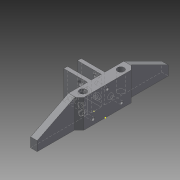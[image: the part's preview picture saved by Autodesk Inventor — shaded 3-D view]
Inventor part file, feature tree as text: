
AUTODESK INVENTOR PART (.ipt)
format: ipt  version: 2015 (Build 190159000, 159)  size: 208,896 bytes
history: native  units: mm
features: sketch x10, extrude x4, hole x4, chamfer x4
ambient origin geometry x8: Origin, YZ Plane, XZ Plane, XY Plane, X Axis, Y Axis, Z Axis, Center Point
bodies: Solid1 (feature_tree)
feature tree (22):
  extrude  "Extrusion1"  Depth=4.0mm
  hole  "Hole1"  [1 undecoded]
  hole  "Hole2"  [1 undecoded]
  chamfer  "Chamfer1"  Distance=5.0mm Angle=45.0deg
  extrude  "Extrusion2"  Depth=60.0mm
  extrude  "Extrusion3"  Depth=60.0mm
  extrude  "Extrusion4"  Depth=30.0mm TaperAngle=0.0deg
  chamfer  "Chamfer2"  Distance=25.0mm
  chamfer  "Chamfer3"  Distance=25.0mm
  chamfer  "Chamfer4"  Distance=30.0mm
  sketch  "Sketch7"  dims[d10=10.0mm]
  hole  "Hole3"  [1 undecoded]
  sketch  "Sketch9"  dims[d12=7.0mm]
  hole  "Hole4"  [1 undecoded]
  sketch  "Sketch1"  dims[d0=10.5mm d1=4.0mm]
  sketch  "Sketch2"  dims[d2=4.0mm d3=12.0mm]
  sketch  "Sketch3"  dims[d4=25.0mm d5=30.0mm d6=0.0mm]
  sketch  "Sketch4"  dims[d7=5.0mm]
  sketch  "Sketch5"  dims[d8=5.0mm]
  sketch  "Sketch6"  dims[d9=5.0mm]
  sketch  "Sketch8"  dims[d11=0.0mm]
  sketch  "Sketch10"  dims[d13=3.0mm d14=6.0mm d15=6.0mm d16=2.0mm d17=90.0deg d18=8.0mm d19=20.594885mm d20=3.0mm d21=6.0mm d22=6.0mm d23=2.0mm d24=90.0deg d25=8.0mm d26=20.594885mm d27=5.0mm d28=2.0mm d29=45.0deg d30=60.0mm d31=60.0mm d32=30.0mm d33=0.0mm d34=25.0mm d35=25.0mm d36=30.0mm d37=0.0mm d38=40.0mm d39=6.0mm d40=6.0mm d41=5.0mm d42=7.0mm d43=7.0mm d44=20.0mm d45=0.0mm d46=5.0mm d47=60.0mm d48=45.0deg d49=20.0mm d50=40.0mm d51=45.0deg d52=20.0mm d53=40.0mm d54=45.0deg d55=30.0mm d56=5.0mm d57=5.0mm d58=15.0mm d59=3.0mm d60=6.0mm d61=6.0mm d62=2.0mm d63=90.0deg d64=20.0mm d65=20.594885mm d66=5.0mm d67=3.0mm d68=6.0mm d69=6.0mm d70=2.0mm d71=90.0deg d72=20.0mm d73=20.594885mm]
note: 4 required parameter values undecoded (feature->parameter linkage not recoverable at this tier; creation-order binding heuristic only, values carry confidence <= 0.55)
